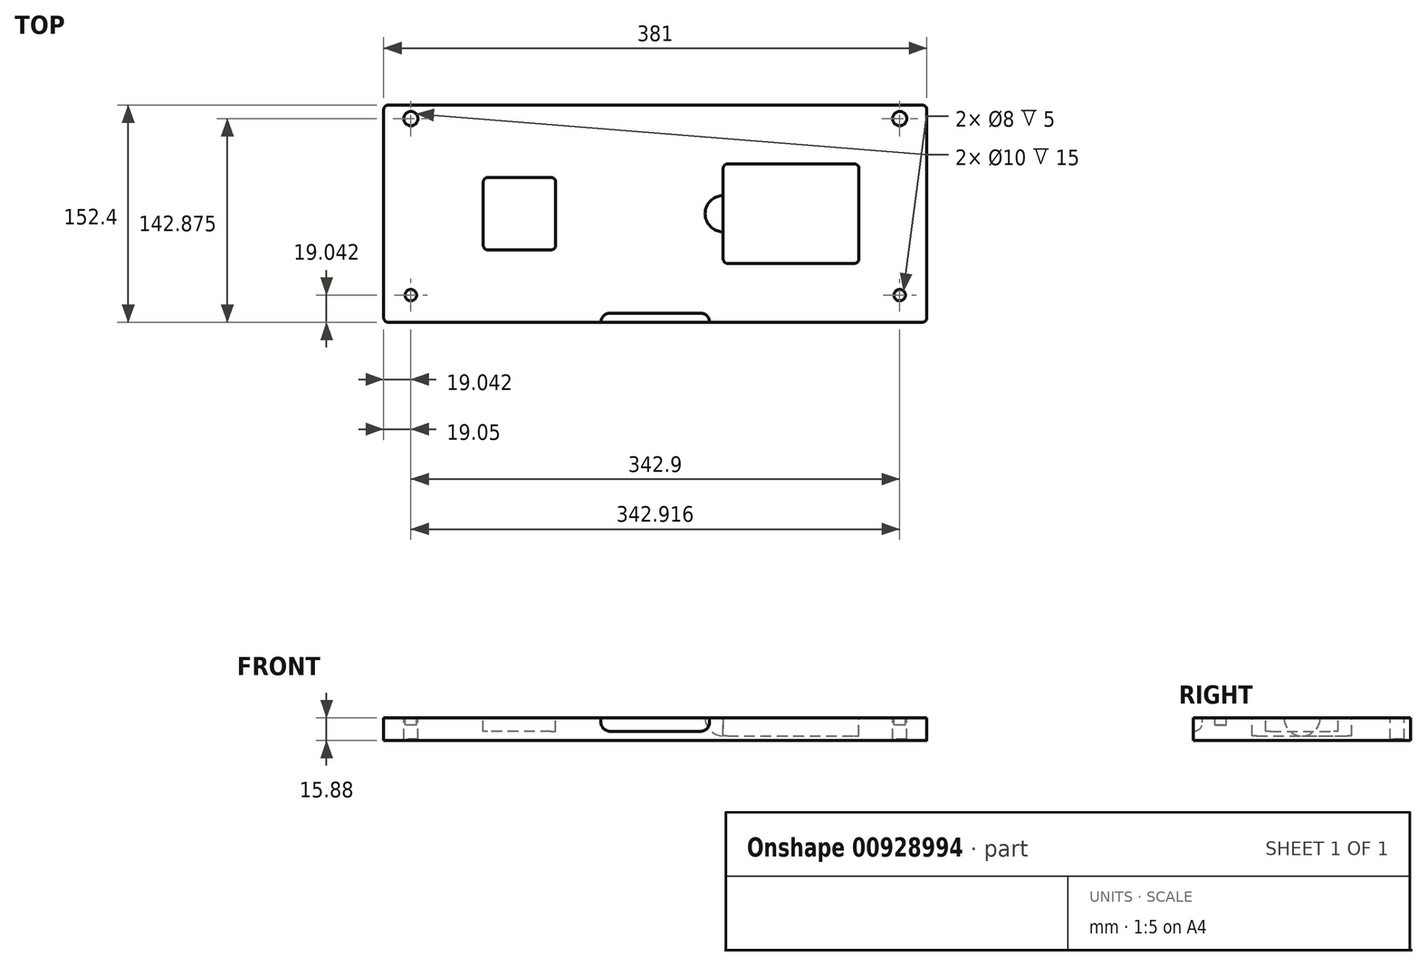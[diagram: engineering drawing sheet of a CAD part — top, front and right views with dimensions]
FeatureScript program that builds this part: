
annotation { "Feature Type Name" : "Feature", "Feature Type Description" : "" }
export const myFeature = defineFeature(function(context is Context, id is Id, definition is map)
    precondition{}
    {
        {
            var Q0;
            Q0=qCreatedBy(makeId("Top.planeOp"),FACE);
            var sketch = newSketch(context, id + "F0", { "sketchPlane" : qUnion([Q0])});
            skLineSegment(sketch, "E0.bottom", {"start": v(190.5, -76.2) * mm, "end": v(-190.5, -76.2) * mm});
            skLineSegment(sketch, "E0.top", {"start": v(190.5, 76.2) * mm, "end": v(-190.5, 76.2) * mm});
            skLineSegment(sketch, "E0.left", {"start": v(190.5, -76.2) * mm, "end": v(190.5, 76.2) * mm});
            skLineSegment(sketch, "E0.right", {"start": v(-190.5, -76.2) * mm, "end": v(-190.5, 76.2) * mm});
            skPoint(sketch, "E0.middle", {"position": v(0, 0) * mm});
            skSolve(sketch);
        }
        {
            var Q0;
            Q0=makeQuery(id+"F0.imprint","IMPRINT",FACE,{"disambiguationData":[TD([[makeQuery(id+"F0.imprint","IMPRINT",EDGE,{"derivedFrom":sQuery(id+"F0.wireOp",EDGE,"E0.bottom")}),-1.0]])]});
            extrude(context, id + "F1", {"entities" : qUnion([Q0]), "oppositeDirection" : true, "depth" : 15.88 * mm, "offsetDistance" : 25.4 * mm});
        }
        {
            var Q0;
            Q0=makeQuery(id+"F1.opExtrude","CAP_FACE",FACE,{"disambiguationData":[OSD([sQuery(id+"F0.wireOp",EDGE,"E0.bottom"),sQuery(id+"F0.wireOp",EDGE,"E0.top"),sQuery(id+"F0.wireOp",EDGE,"E0.left"),sQuery(id+"F0.wireOp",EDGE,"E0.right")])],"isStart":true});
            var sketch = newSketch(context, id + "F2", { "sketchPlane" : qUnion([Q0])});
            skLineSegment(sketch, "E1.bottom", {"start": v(47.62, -34.92) * mm, "end": v(142.88, -34.92) * mm});
            skLineSegment(sketch, "E1.top", {"start": v(47.62, 34.93) * mm, "end": v(142.88, 34.93) * mm});
            skLineSegment(sketch, "E1.left", {"start": v(47.62, -34.92) * mm, "end": v(47.62, 34.93) * mm});
            skLineSegment(sketch, "E1.right", {"start": v(142.88, -34.92) * mm, "end": v(142.88, 34.93) * mm});
            skPoint(sketch, "E1.middle", {"position": v(95.25, 0) * mm});
            skLineSegment(sketch, "E2.bottom", {"start": v(-69.85, -25.4) * mm, "end": v(-120.65, -25.4) * mm});
            skLineSegment(sketch, "E2.top", {"start": v(-69.85, 25.4) * mm, "end": v(-120.65, 25.4) * mm});
            skLineSegment(sketch, "E2.left", {"start": v(-69.85, -25.4) * mm, "end": v(-69.85, 25.4) * mm});
            skLineSegment(sketch, "E2.right", {"start": v(-120.65, -25.4) * mm, "end": v(-120.65, 25.4) * mm});
            skPoint(sketch, "E2.middle", {"position": v(-95.25, 0) * mm});
            skLineSegment(sketch, "E3", {"start": v(0, 0) * mm, "end": v(95.25, 0) * mm});
            skLineSegment(sketch, "E4", {"start": v(0, 0) * mm, "end": v(-95.25, 0) * mm});
            skSolve(sketch);
        }
        {
            var Q0;
            Q0=makeQuery(id+"F2.imprint","IMPRINT",FACE,{"disambiguationData":[TD([[makeQuery(id+"F2.imprint","IMPRINT",EDGE,{"derivedFrom":sQuery(id+"F2.wireOp",EDGE,"E2.bottom")}),-1.0]])]});
            extrude(context, id + "F3", {"entities" : qUnion([Q0]), "operationType" : NewBodyOperationType.REMOVE, "oppositeDirection" : true, "depth" : 9.52 * mm, "offsetDistance" : 25.4 * mm});
        }
        {
            var Q0;
            Q0=makeQuery(id+"F2.imprint","IMPRINT",FACE,{"disambiguationData":[TD([[makeQuery(id+"F2.imprint","IMPRINT",EDGE,{"derivedFrom":sQuery(id+"F2.wireOp",EDGE,"E1.bottom")}),1.0]])]});
            extrude(context, id + "F4", {"entities" : qUnion([Q0]), "operationType" : NewBodyOperationType.REMOVE, "oppositeDirection" : true, "depth" : 12.7 * mm, "offsetDistance" : 25.4 * mm});
        }
        {
            var Q0;
            Q0=makeQuery(id+"F3.boolean.opBoolean","COPY",EDGE,{"derivedFrom":makeQuery(id+"F3.opExtrude","SWEPT_EDGE",EDGE,{"disambiguationData":[OSD([sQuery(id+"F2.wireOp",EDGE,"E2.top"),sQuery(id+"F2.wireOp",EDGE,"E2.left")])]})});
            var Q1;
            Q1=makeQuery(id+"F4.boolean.opBoolean","COPY",EDGE,{"derivedFrom":makeQuery(id+"F4.opExtrude","SWEPT_EDGE",EDGE,{"disambiguationData":[OSD([sQuery(id+"F2.wireOp",EDGE,"E1.top"),sQuery(id+"F2.wireOp",EDGE,"E1.right")])]})});
            var Q2;
            Q2=makeQuery(id+"F3.boolean.opBoolean","COPY",EDGE,{"derivedFrom":makeQuery(id+"F3.opExtrude","SWEPT_EDGE",EDGE,{"disambiguationData":[OSD([sQuery(id+"F2.wireOp",EDGE,"E2.bottom"),sQuery(id+"F2.wireOp",EDGE,"E2.left")])]})});
            var Q3;
            Q3=makeQuery(id+"F4.boolean.opBoolean","COPY",EDGE,{"derivedFrom":makeQuery(id+"F4.opExtrude","SWEPT_EDGE",EDGE,{"disambiguationData":[OSD([sQuery(id+"F2.wireOp",EDGE,"E1.bottom"),sQuery(id+"F2.wireOp",EDGE,"E1.right")])]})});
            var Q4;
            Q4=makeQuery(id+"F3.boolean.opBoolean","COPY",EDGE,{"derivedFrom":makeQuery(id+"F3.opExtrude","SWEPT_EDGE",EDGE,{"disambiguationData":[OSD([sQuery(id+"F2.wireOp",EDGE,"E2.bottom"),sQuery(id+"F2.wireOp",EDGE,"E2.right")])]})});
            var Q5;
            Q5=makeQuery(id+"F4.boolean.opBoolean","COPY",EDGE,{"derivedFrom":makeQuery(id+"F4.opExtrude","SWEPT_EDGE",EDGE,{"disambiguationData":[OSD([sQuery(id+"F2.wireOp",EDGE,"E1.bottom"),sQuery(id+"F2.wireOp",EDGE,"E1.left")])]})});
            var Q6;
            Q6=makeQuery(id+"F4.boolean.opBoolean","COPY",EDGE,{"derivedFrom":makeQuery(id+"F4.opExtrude","SWEPT_EDGE",EDGE,{"disambiguationData":[OSD([sQuery(id+"F2.wireOp",EDGE,"E1.top"),sQuery(id+"F2.wireOp",EDGE,"E1.left")])]})});
            var Q7;
            Q7=makeQuery(id+"F3.boolean.opBoolean","COPY",EDGE,{"derivedFrom":makeQuery(id+"F3.opExtrude","SWEPT_EDGE",EDGE,{"disambiguationData":[OSD([sQuery(id+"F2.wireOp",EDGE,"E2.top"),sQuery(id+"F2.wireOp",EDGE,"E2.right")])]})});
            fillet(context, id + "F5", {"entities" : qUnion([Q0, Q1, Q2, Q3, Q4, Q5, Q6, Q7]), "radius" : 3.17 * mm, "tangentPropagation" : true, "allowEdgeOverflow" : false});
        }
        {
            var Q0;
            Q0=makeQuery(id+"F1.opExtrude","CAP_FACE",FACE,{"disambiguationData":[OSD([sQuery(id+"F0.wireOp",EDGE,"E0.bottom"),sQuery(id+"F0.wireOp",EDGE,"E0.top"),sQuery(id+"F0.wireOp",EDGE,"E0.left"),sQuery(id+"F0.wireOp",EDGE,"E0.right")])],"isStart":true});
            var sketch = newSketch(context, id + "F6", { "sketchPlane" : qUnion([Q0])});
            skCircle(sketch, "E5", {"center": v(-171.46, -57.16) * mm, "radius": 4 * mm});
            skCircle(sketch, "E6", {"center": v(171.46, -57.16) * mm, "radius": 4 * mm});
            skSolve(sketch);
        }
        {
            var Q0;
            Q0=makeQuery(id+"F6.imprint","IMPRINT",FACE,{"disambiguationData":[TD([[makeQuery(id+"F6.imprint","IMPRINT",EDGE,{"derivedFrom":sQuery(id+"F6.wireOp",EDGE,"E5")}),1.0]])]});
            var Q1;
            Q1=makeQuery(id+"F6.imprint","IMPRINT",FACE,{"disambiguationData":[TD([[makeQuery(id+"F6.imprint","IMPRINT",EDGE,{"derivedFrom":sQuery(id+"F6.wireOp",EDGE,"E6")}),1.0]])]});
            extrude(context, id + "F7", {"entities" : qUnion([Q0, Q1]), "operationType" : NewBodyOperationType.REMOVE, "oppositeDirection" : true, "depth" : 5 * mm, "offsetDistance" : 25.4 * mm});
        }
        {
            var Q0;
            Q0=makeQuery(id+"F1.opExtrude","SWEPT_FACE",FACE,{"disambiguationData":[OSD([sQuery(id+"F0.wireOp",EDGE,"E0.bottom")])]});
            var sketch = newSketch(context, id + "F8", { "sketchPlane" : qUnion([Q0])});
            skLineSegment(sketch, "E7.bottom", {"start": v(38.1, -9.52) * mm, "end": v(-38.1, -9.53) * mm});
            skLineSegment(sketch, "E7.top", {"start": v(38.1, 9.53) * mm, "end": v(-38.1, 9.52) * mm});
            skLineSegment(sketch, "E7.left", {"start": v(38.1, -9.52) * mm, "end": v(38.1, 9.53) * mm});
            skLineSegment(sketch, "E7.right", {"start": v(-38.1, -9.53) * mm, "end": v(-38.1, 9.53) * mm});
            skPoint(sketch, "E7.middle", {"position": v(0, 0) * mm});
            skSolve(sketch);
        }
        {
            var Q0;
            {var subQ0=sQuery(id+"F8.wireOp",EDGE,"E7.bottom");Q0=makeQuery(id+"F8.imprint","IMPRINT",FACE,{"disambiguationData":[TD([[makeQuery(id+"F8.imprint","IMPRINT",EDGE,{"derivedFrom":subQ0}),-1.0]])]});}
            extrude(context, id + "F9", {"entities" : qUnion([Q0]), "operationType" : NewBodyOperationType.REMOVE, "oppositeDirection" : true, "depth" : 6.35 * mm, "offsetDistance" : 25.4 * mm});
        }
        {
            var Q0;
            Q0=makeQuery(id+"F9.boolean.opBoolean","COPY",EDGE,{"derivedFrom":makeQuery(id+"F9.opExtrude","SWEPT_EDGE",EDGE,{"disambiguationData":[OSD([sQuery(id+"F8.wireOp",EDGE,"E7.bottom"),sQuery(id+"F8.wireOp",EDGE,"E7.right")])]})});
            var Q1;
            Q1=makeQuery(id+"F9.boolean.opBoolean","COPY",EDGE,{"derivedFrom":makeQuery(id+"F9.opExtrude","CAP_EDGE",EDGE,{"disambiguationData":[OSD([sQuery(id+"F8.wireOp",EDGE,"E7.right")])],"isStart":false})});
            var Q2;
            Q2=makeQuery(id+"F9.boolean.opBoolean","COPY",EDGE,{"derivedFrom":makeQuery(id+"F9.opExtrude","CAP_EDGE",EDGE,{"disambiguationData":[OSD([sQuery(id+"F8.wireOp",EDGE,"E7.bottom")])],"isStart":false})});
            var Q3;
            Q3=makeQuery(id+"F9.boolean.opBoolean","COPY",EDGE,{"derivedFrom":makeQuery(id+"F9.opExtrude","SWEPT_EDGE",EDGE,{"disambiguationData":[OSD([sQuery(id+"F8.wireOp",EDGE,"E7.bottom"),sQuery(id+"F8.wireOp",EDGE,"E7.left")])]})});
            var Q4;
            Q4=makeQuery(id+"F9.boolean.opBoolean","COPY",EDGE,{"derivedFrom":makeQuery(id+"F9.opExtrude","CAP_EDGE",EDGE,{"disambiguationData":[OSD([sQuery(id+"F8.wireOp",EDGE,"E7.left")])],"isStart":false})});
            fillet(context, id + "F10", {"entities" : qUnion([Q0, Q1, Q2, Q3, Q4]), "radius" : 6.35 * mm, "tangentPropagation" : true, "allowEdgeOverflow" : false});
        }
        {
            var Q0;
            Q0=makeQuery(id+"F1.opExtrude","CAP_FACE",FACE,{"disambiguationData":[OSD([sQuery(id+"F0.wireOp",EDGE,"E0.bottom"),sQuery(id+"F0.wireOp",EDGE,"E0.top"),sQuery(id+"F0.wireOp",EDGE,"E0.left"),sQuery(id+"F0.wireOp",EDGE,"E0.right")])],"isStart":true});
            var sketch = newSketch(context, id + "F11", { "sketchPlane" : qUnion([Q0])});
            skCircle(sketch, "E8", {"center": v(-171.45, 66.67) * mm, "radius": 5 * mm});
            skCircle(sketch, "E9", {"center": v(171.45, 66.68) * mm, "radius": 5 * mm});
            skSolve(sketch);
        }
        {
            var Q0;
            Q0=makeQuery(id+"F11.imprint","IMPRINT",FACE,{"disambiguationData":[TD([[makeQuery(id+"F11.imprint","IMPRINT",EDGE,{"derivedFrom":sQuery(id+"F11.wireOp",EDGE,"E8")}),1.0]])]});
            var Q1;
            Q1=makeQuery(id+"F11.imprint","IMPRINT",FACE,{"disambiguationData":[TD([[makeQuery(id+"F11.imprint","IMPRINT",EDGE,{"derivedFrom":sQuery(id+"F11.wireOp",EDGE,"E9")}),1.0]])]});
            extrude(context, id + "F12", {"entities" : qUnion([Q0, Q1]), "operationType" : NewBodyOperationType.REMOVE, "oppositeDirection" : true, "depth" : 15 * mm, "offsetDistance" : 25 * mm});
        }
        {
            var Q0;
            Q0=makeQuery(id+"F1.opExtrude","SWEPT_EDGE",EDGE,{"disambiguationData":[OSD([sQuery(id+"F0.wireOp",EDGE,"E0.bottom"),sQuery(id+"F0.wireOp",EDGE,"E0.right")])]});
            var Q1;
            Q1=makeQuery(id+"F1.opExtrude","SWEPT_EDGE",EDGE,{"disambiguationData":[OSD([sQuery(id+"F0.wireOp",EDGE,"E0.bottom"),sQuery(id+"F0.wireOp",EDGE,"E0.left")])]});
            var Q2;
            Q2=makeQuery(id+"F1.opExtrude","SWEPT_EDGE",EDGE,{"disambiguationData":[OSD([sQuery(id+"F0.wireOp",EDGE,"E0.top"),sQuery(id+"F0.wireOp",EDGE,"E0.left")])]});
            var Q3;
            Q3=makeQuery(id+"F1.opExtrude","SWEPT_EDGE",EDGE,{"disambiguationData":[OSD([sQuery(id+"F0.wireOp",EDGE,"E0.top"),sQuery(id+"F0.wireOp",EDGE,"E0.right")])]});
            fillet(context, id + "F13", {"entities" : qUnion([Q0, Q1, Q2, Q3]), "radius" : 3.17 * mm, "tangentPropagation" : true, "allowEdgeOverflow" : false});
        }
        {
            var Q0;
            Q0=makeQuery(id+"F1.opExtrude","CAP_FACE",FACE,{"disambiguationData":[OSD([sQuery(id+"F0.wireOp",EDGE,"E0.bottom"),sQuery(id+"F0.wireOp",EDGE,"E0.top"),sQuery(id+"F0.wireOp",EDGE,"E0.left"),sQuery(id+"F0.wireOp",EDGE,"E0.right")])],"isStart":true});
            var sketch = newSketch(context, id + "F14", { "sketchPlane" : qUnion([Q0])});
            skArc(sketch, "E10", {"start": v(47.62, 12.7) * mm, "mid": v(34.92, 0) * mm, "end": v(47.62, -12.7) * mm});
            skLineSegment(sketch, "E11", {"start": v(47.62, 12.7) * mm, "end": v(47.62, -12.7) * mm});
            skSolve(sketch);
        }
        {
            var Q0;
            Q0=makeQuery(id+"F14.imprint","IMPRINT",FACE,{"disambiguationData":[TD([[makeQuery(id+"F14.imprint","IMPRINT",EDGE,{"derivedFrom":sQuery(id+"F14.wireOp",EDGE,"E10")}),1.0]])]});
            var Q1;
            Q1=sQuery(id+"F14.wireOp",EDGE,"E11");
            revolve(context, id + "F15", {"operationType" : NewBodyOperationType.REMOVE, "surfaceOperationType" : NewSurfaceOperationType.NEW, "entities" : qUnion([Q0]), "axis" : qUnion([Q1]), "revolveType" : RevolveType.FULL, "oppositeDirection" : true});
        }
    });
